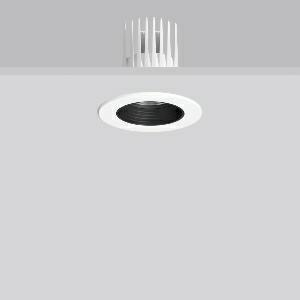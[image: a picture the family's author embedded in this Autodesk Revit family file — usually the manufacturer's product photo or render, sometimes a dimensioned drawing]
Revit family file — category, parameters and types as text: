
# Revit family: heledon_mini_e_901746_002_1_76_8e38
name_source: partatom
category: Lighting Fixtures
units: mm (PartAtom-declared; Revit-internal decimal feet)

## family parameters
Cut with Voids When Loaded = No
Host = Face
Light Source = No
Part Type = Normal
Room Calculation Point = No
Round Connector Dimension = Use Diameter
Shared = No

## types (1)
- HELEDON mini E (1 x LED Modul 940, 2450 lm, 4000)
    Apparent Load = 20 VA
    Approval mark = CE
    CIE Flux Codes = 80 99 100 100 100
    Color Rendering = 92
    Color Temperature = 4000
    Default Elevation = 1800 mm
    Description = Series: HELEDON mini
Round recessed downlight. Housing: die-cast aluminium, powder-coated. Black plastic ring and recessed LED to prevent glare from the side. Optical assembly with lens made of plastic (polycarbonate) for the best homogeneous light distribution - can be changed without tools. Best colour rendering index Ra>90. Suitable for Recessed ceiling mounting. Installation without tools thanks to spring fastening system. Including separate LED converter with connecting cable 600 mm.High quality converter without flickering and stroboscopic effect. Through-wiring box (5 pole) available as accessory. The following accessories can be mounted without use of tools: interchangeable lenses, decorative glasses, honeycomb louvre, clear and frosted diffusers, white interchangeable plastic ring. 
Colour: traffic white, matt (RAL 9016)
Diameter: 124 mm
Height: 3 mm
Cut-out diameter: 114 mm
Recess height: 170 mm
Luminaire: recess height: 120 mm
Lamp: LED
Socket: without socket
Colour temperature: 4000K
Colour rendering index (CRI): 92
System power: 20 W
Rated luminous flux: 2450 lm
Luminous efficiency: 123 lm/W
Control gear: Converter, dimmable, DALI
Protection class: II
Type of protection: IP 20
    Height = 0 mm  [stored 0 ft]
    Lamp = 1 x LED Modul 940
    Lamp Light Flux = 2450 lm
    Lamp count = 1
    Length = 124 mm  [stored 0.406824 ft]
    Lifetime = 50000 h
    Luminous efficacy = 123 lm/W
    Manufacturer = RZB
    ModVariant = No
    Model = 901746.002.1.76
    Mounting Place = Ceiling
    Mounting Type = Recessed
    Number of Poles = 1
    OnlyDefault = Yes
    Power Factor = 1
    Product Name = HELEDON mini E
    Product group = Recessed downlights
    ProductGroupID = 402
    Protection Class = Protection class II
    Protection Degree = IP 20
    RLX_Detail_Level = 1
    RLX_Emergency_Light_Flux = 0 lm
    RLX_Emergency_Type = 0
    RLX_Emergency_Type_DB = No
    RlxData = <blob elided: 124349 chars, md5=5ec64696>
    Socket = socket
    Standby Power = 0 W
    System Light Flux = 2450 lm
    System Power = 20 W
    Type Comments = Product without accessories
    Type Image = 901656.002.jpg
    URL = http://relux.com
    VarID = ---
    Voltage = 230 V
    Voltage Range = 220-240 V
    Weight = 0.00 kg
    Width = 0 mm  [stored 0 ft]

note: [stored X ft] marks values corroborated as IEEE doubles in the binary element streams (Revit-internal decimal feet)

## geometry (parser evidence)
native form markers: Blend x4, Sweep x11
no freeform markers — native parametric forms only
